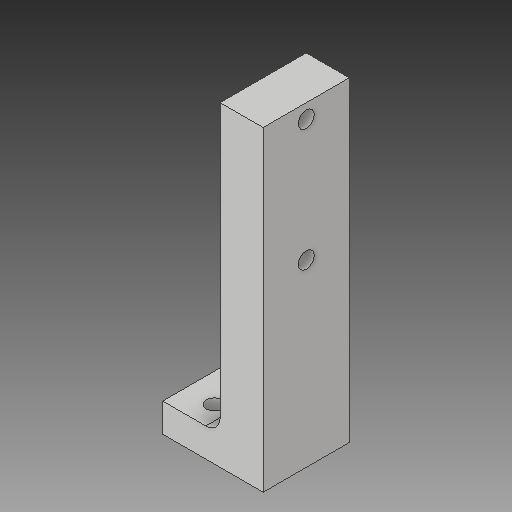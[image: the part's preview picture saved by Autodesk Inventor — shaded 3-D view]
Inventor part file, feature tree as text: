
AUTODESK INVENTOR PART (.ipt)
format: ipt  version: 2019 (Build 230136000, 136)  size: 135,680 bytes
history: native  units: in
note: dims shown in document units (in); Inventor stores cm internally (conversion verified against a paired STEP export)
features: sketch x4, projected_geometry x3, extrude x2, hole x2, fillet x1
ambient origin geometry x8: Origin, YZ Plane, XZ Plane, XY Plane, X Axis, Y Axis, Z Axis, Center Point
bodies: Solid1 (feature_tree)
feature tree (12):
  extrude  "Extrusion1"  Depth=2.75in
  hole  "Hole1"  [1 undecoded]
  extrude  "Extrusion2"  Depth=2.75in
  hole  "Hole3"  [1 undecoded]
  fillet  "Fillet1"  Radius=0.375in
  sketch  "Sketch1"  dims[d0=0.75in d1=2.75in]
  sketch  "Sketch2"  dims[d2=0.375in d3=0.0in d4=1.061in]
  projected_geometry  "Projected Loop1"
  sketch  "Sketch5"  dims[d5=0.75in d6=2.75in]
  projected_geometry  "Projected Loop3"
  sketch  "Sketch6"  dims[d7=0.125in d8=0.375in d9=0.375in d10=0.14in d11=0.75in d12=0.375in d13=0.25in d14=0.5635in d15=1.0in d16=0.8108in d31=0.25in d32=0.5in d33=0.0in d34=0.75in d35=0.2in d36=0.2in d37=0.14in d38=0.75in d39=0.375in d40=0.25in d41=0.5635in d42=1.0in d43=0.8108in d44=0.125in]
  projected_geometry  "Projected Loop4"
note: 2 required parameter values undecoded (feature->parameter linkage not recoverable at this tier; creation-order binding heuristic only, values carry confidence <= 0.55)
